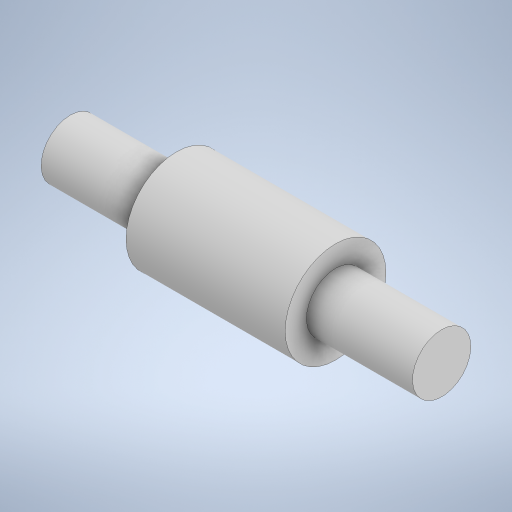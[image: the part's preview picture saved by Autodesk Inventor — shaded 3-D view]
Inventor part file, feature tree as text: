
AUTODESK INVENTOR PART (.ipt)
format: ipt  version: 2024 (Build 280153000, 153)  size: 242,688 bytes
history: native  units: mm
features: extrude x2, other x1, sketch x1
ambient origin geometry x8: Origin, YZ Plane, XZ Plane, XY Plane, X Axis, Y Axis, Z Axis, Center Point
bodies: Body1 (feature_tree)
feature tree (4):
  other  "Sólido1"
  sketch  "Boceto1"  dims[d0=19.0mm d1=11.0mm d2=70.0mm d3=0.0mm d4=30.0mm d5=0.0mm]
  extrude  "Extrusión1"  Depth=30.0mm
  extrude  "Extrusión2"  Depth=70.0mm TaperAngle=0.0deg
